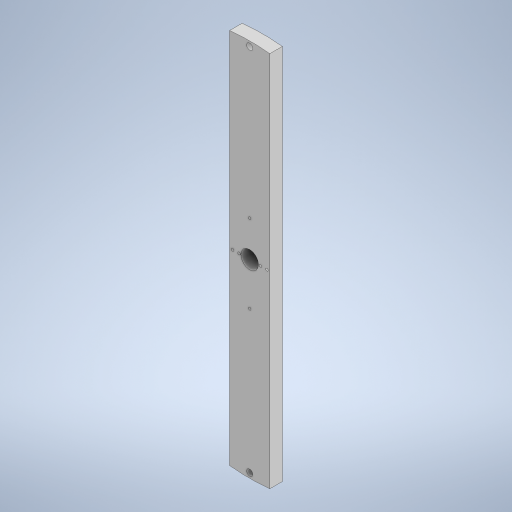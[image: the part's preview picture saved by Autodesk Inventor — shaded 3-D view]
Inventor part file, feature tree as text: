
AUTODESK INVENTOR PART (.ipt)
format: ipt  version: 2023.1 (Build 271208000, 208)  size: 258,048 bytes
history: native  units: mm
features: other x1, extrude x1, sketch x1
ambient origin geometry x8: Origin, YZ Plane, XZ Plane, XY Plane, X Axis, Y Axis, Z Axis, Center Point
bodies: Body1 (feature_tree)
feature tree (3):
  other  "솔리드1"
  extrude  "돌출1"  Depth=16.0mm
  sketch  "스케치1"
